# Revit family: Front_Load_Mailbox-Florence_Manufacturing-5High_Suite
name_source: partatom
category: Generic Models
revit_build: Autodesk Revit Architecture 2012 (Build: 20110916_2132(x64)
units: mm (PartAtom-declared; Revit-internal decimal feet)

## types (6) — shared parameters
Description = Front Load Mailbox
Door Material = Metal - Florence - Paint - Antique Bronze
Hardware = Metal - Florence - Steel
Height = 1' - 7 3/4"
Manufacturer = Florence Manufacturing
Minimum USPS Access Door = 2' - 4"
Mullion = 0' - 1 7/16"
Product Name = STD-4C
R Slot 2 = Empty
Unit Casing = Metal - Florence - Paint - Antique Bronze
Unit Casing Width = 1' - 6 13/16"
Width = 1' - 5"

## per-type parameters (varying)
| type | Center Mullion | Length | R Slot 1-Top | R Slot 3 | R Slot 4 | R Slot 5 | Side Frame Thickness | Slot 1-Top | Slot 2 | Slot 3 | Slot 4 | Slot 5 | URL |
| 4C05D-08 | Yes | 2' - 6 5/16" | Single Tenant Door | Letter Drop | Single Tenant Door | Single Tenant Door | 0' - 2 3/16" | Single Tenant Door | Single Tenant Door | Single Tenant Door | Single Tenant Door | Single Tenant Door | http://www.florencemailboxes.com |
| 4C05S-03 | No | 1' - 4 1/4" | Empty | Empty | Empty | Empty | 0' - 2 5/16" | Single Tenant Door | Single Tenant Door | Single Tenant Door | Single Tenant Door | Single Tenant Door |  |
| 4C05S-1P | No | 1' - 4 1/4" | Empty | Empty | Empty | Empty | 0' - 2 5/16" | Empty | Empty | Empty | Empty | Five High Single Parcel Locker |  |
| 4C05D-2P | Yes | 2' - 6 5/16" | Empty | Empty | Empty | Five High Single Parcel Locker | 0' - 2 3/16" | Empty | Empty | Empty | Empty | Five High Single Parcel Locker |  |
| 4C05D-03 | Yes | 2' - 6 5/16" | Single Tenant Door | Letter Drop | Single Tenant Door | Single Tenant Door | 0' - 2 3/16" | Empty | Empty | Empty | Empty | Five High Single Parcel Locker | http://www.florencemailboxes.com |
| 4C05D-07 | Yes | 2' - 6 5/16" | Single Tenant Door | Empty | Three High Letter Drop | Single Tenant Door | 0' - 2 3/16" | Single Tenant Door | Single Tenant Door | Single Tenant Door | Single Tenant Door | Single Tenant Door | http://www.florencemailboxes.com |

note: column(s) folded — value = type name in every type: Model

## geometry (parser evidence)
native form markers: Blend x5, Sweep x16
no freeform markers — native parametric forms only
